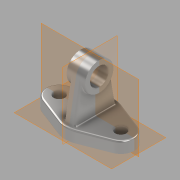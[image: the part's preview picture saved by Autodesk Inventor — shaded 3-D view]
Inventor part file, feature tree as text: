
AUTODESK INVENTOR PART (.ipt)
format: ipt  version: 2020 (Build 240168000, 168)  size: 226,816 bytes
history: native  units: mm
features: sketch x4, extrude x3, other x1, hole x1, fillet x1
ambient origin geometry x8: Origin, YZ Plane, XZ Plane, XY Plane, X Axis, Y Axis, Z Axis, Center Point
bodies: Body1 (feature_tree)
feature tree (10):
  other  "Sólido1"
  extrude  "PlacaBase"  Depth=44.0mm
  extrude  "Mástil"  Depth=18.0mm
  extrude  "CírculoSuperior"  Depth=18.0mm TaperAngle=0.0deg
  hole  "Agujero1"  [1 undecoded]
  fillet  "Empalme1"  Radius=46.0mm
  sketch  "Boceto1"  dims[d0=80.0mm d1=44.0mm]
  sketch  "Boceto2"  dims[d2=40.0mm d3=18.0mm]
  sketch  "Boceto3"  dims[d4=50.0mm d5=18.0mm d6=0.0mm]
  sketch  "Boceto4"  dims[d7=40.0mm d8=40.0mm d9=46.0mm d10=76.0mm d11=67.0mm d12=33.5mm d13=17.0mm d14=0.0mm d15=30.0mm d16=0.0mm d17=30.0mm d18=6.0mm d19=4.0mm d20=2.0mm d21=90.0deg d22=8.0mm d23=20.594885mm d24=3.0mm]
note: 1 required parameter value undecoded (feature->parameter linkage not recoverable at this tier; creation-order binding heuristic only, values carry confidence <= 0.55)
